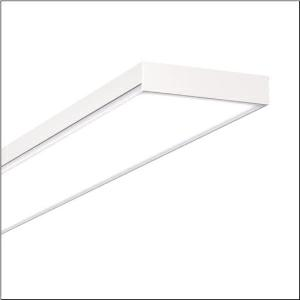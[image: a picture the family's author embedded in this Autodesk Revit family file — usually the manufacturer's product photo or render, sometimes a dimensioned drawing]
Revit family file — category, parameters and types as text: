
# Revit family: apollon_31_surface_51mp25wm2441wa
name_source: partatom
category: Lighting Fixtures
units: mm (PartAtom-declared; Revit-internal decimal feet)

## family parameters
Cut with Voids When Loaded = No
Host = Face
Light Source = No
Part Type = Normal
Room Calculation Point = No
Round Connector Dimension = Use Diameter
Shared = No

## types (1)
- Apollon 31 Surface (1 x LED, 3800 lm, 27 W, 4000K)
    Apparent Load = 27 VA
    CIE Flux Codes = 61 87 97 97 100
    Color Rendering = 80
    Color Temperature = 4000K
    Default Elevation = 1800 mm
    Description = Apollon 31 Surface, office luminaire, primary optical cover: micro prismatic cover, of PMMA, light emission: direct distribution, primary light characteristic: symmetric, installation type: surface-mounted, LED, rated luminous flux: 3.800lm, luminous efficacy: 139lm/W, light colour: 840, colour temperature: 4000K, control gear: ON/OFF Multilumen, with terminal, 3-pole, mains connection: 220..240V, AC, 50/60Hz, rated input power: 27W, housing, of sheet steel, coated, traffic white (RAL 9016), length: 1.245mm, width: 200mm, height: 44mm, protection rating (complete): IP20, protection rating (on room side): IP40, protection rating (lamp compartment, on room side): IP40, insulation class (complete): insulation class I (protective earthing), certification: CE, ENEC, UKCA, impact resistance: IK02, permissible operating ambient temperature: -20..+40°C, packaging unit: 1 piece
    Height = 44 mm
    Lamp = 1 x LED
    Lamp Light Flux = 3800 lm
    Lamp Power = 27 W
    Lamp count = 1
    Length = 1245 mm
    Luminous efficacy = 141 lm/W
    Manufacturer = Siteco
    ModVariant = No
    Model = 51MP25WM2441WA
    Mounting Place = Ceiling
    Mounting Type = Surface mounted
    Number of Poles = 1
    OnlyDefault = Yes
    Power Factor = 1
    Product Name = Apollon 31 Surface
    Product group = office luminaire | ceiling mounted
    ProductGroupID = 301
    Protection Class = Protection class I
    Protection Degree = IP 20
    RLX_Detail_Level = 1
    RLX_Emergency_Light_Flux = 0 lm
    RLX_Emergency_Type = 0
    RLX_Emergency_Type_DB = No
    RlxData = <blob elided: 20797 chars, md5=4548d823>
    Socket = socket
    Standby Power = 0 W
    System Light Flux = 3800 lm
    System Power = 27 W
    Type Comments = Product without accessories
    Type Image = l_1313658.jpg
    URL = http://relux.com
    VarID = ---
    Voltage = 0 V
    Weight = 0.00 kg
    Width = 200 mm  [stored 0.656168 ft]

note: [stored X ft] marks values corroborated as IEEE doubles in the binary element streams (Revit-internal decimal feet)

## geometry (parser evidence)
native form markers: Blend x4, Sweep x11
no freeform markers — native parametric forms only
